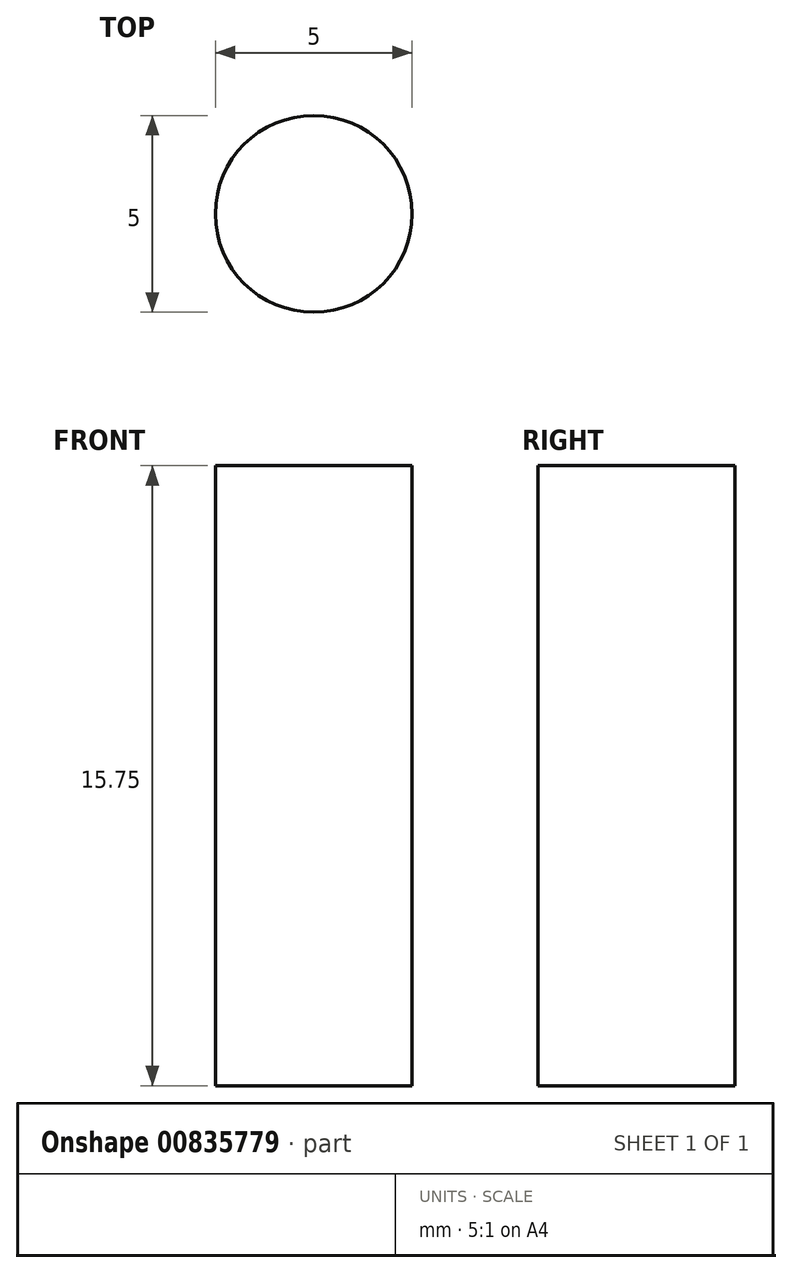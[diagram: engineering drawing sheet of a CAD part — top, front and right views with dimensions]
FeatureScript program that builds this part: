
annotation { "Feature Type Name" : "Feature", "Feature Type Description" : "" }
export const myFeature = defineFeature(function(context is Context, id is Id, definition is map)
    precondition{}
    {
        {
            var Q0;
            Q0=qCreatedBy(makeId("Top.planeOp"),FACE);
            var sketch = newSketch(context, id + "F0", { "sketchPlane" : qUnion([Q0])});
            skLineSegment(sketch, "E0.bottom", {"start": v(-18, 18.3) * mm, "end": v(18, 18.3) * mm, "construction": true});
            skLineSegment(sketch, "E0.top", {"start": v(-13, -18.3) * mm, "end": v(13, -18.3) * mm});
            skLineSegment(sketch, "E0.left", {"start": v(-18, 18.3) * mm, "end": v(-18, -13.3) * mm});
            skLineSegment(sketch, "E0.right", {"start": v(18, 18.3) * mm, "end": v(18, -13.3) * mm});
            skArc(sketch, "E1", {"start": v(18, 18.3) * mm, "mid": v(0, 36.3) * mm, "end": v(-18, 18.3) * mm});
            skLineSegment(sketch, "E2", {"start": v(-18, 0) * mm, "end": v(0, 0) * mm, "construction": true});
            skLineSegment(sketch, "E3", {"start": v(0, 0) * mm, "end": v(18, 0) * mm, "construction": true});
            skPoint(sketch, "E4", {"position": v(0, 36.3) * mm});
            skPoint(sketch, "E5.visualSharp", {"position": v(-18, -18.3) * mm});
            skArc(sketch, "E5.filletArc", {"start": v(-18, -13.3) * mm, "mid": v(-16.54, -16.84) * mm, "end": v(-13, -18.3) * mm});
            skPoint(sketch, "E6.visualSharp", {"position": v(18, -18.3) * mm});
            skArc(sketch, "E6.filletArc", {"start": v(13, -18.3) * mm, "mid": v(16.54, -16.84) * mm, "end": v(18, -13.3) * mm});
            skSolve(sketch);
        }
        {
            var Q0;
            Q0 = qSketchRegion(id + "F0", true);
            extrude(context, id + "F1", {"entities" : qUnion([Q0]), "depth" : 15.75 * mm, "offsetDistance" : 25 * mm});
        }
        {
            var Q0;
            Q0=makeQuery(id+"F1.opExtrude","CAP_FACE",FACE,{"disambiguationData":[OSD([sQuery(id+"F0.wireOp",EDGE,"E0.top"),sQuery(id+"F0.wireOp",EDGE,"E0.left"),sQuery(id+"F0.wireOp",EDGE,"E0.right"),sQuery(id+"F0.wireOp",EDGE,"E1")])],"isStart":false});
            var sketch = newSketch(context, id + "F2", { "sketchPlane" : qUnion([Q0])});
            skCircle(sketch, "E7", {"center": v(0, 27.3) * mm, "radius": 2.5 * mm});
            skCircle(sketch, "E8", {"center": v(11, 6.2) * mm, "radius": 2.5 * mm});
            skCircle(sketch, "E9.MirrorC", {"center": v(-11, 6.2) * mm, "radius": 2.5 * mm});
            skSolve(sketch);
        }
        {
            var Q0;
            Q0=makeQuery(id+"F2.imprint","IMPRINT",FACE,{"disambiguationData":[TD([[makeQuery(id+"F2.imprint","IMPRINT",EDGE,{"derivedFrom":sQuery(id+"F2.wireOp",EDGE,"E7")}),1.0]])]});
            var Q1;
            Q1=makeQuery(id+"F2.imprint","IMPRINT",FACE,{"disambiguationData":[TD([[makeQuery(id+"F2.imprint","IMPRINT",EDGE,{"derivedFrom":sQuery(id+"F2.wireOp",EDGE,"E9.MirrorC")}),-1.0]])]});
            var Q2;
            Q2=makeQuery(id+"F2.imprint","IMPRINT",FACE,{"disambiguationData":[TD([[makeQuery(id+"F2.imprint","IMPRINT",EDGE,{"derivedFrom":sQuery(id+"F2.wireOp",EDGE,"E8")}),1.0]])]});
            extrude(context, id + "F3", {"entities" : qUnion([Q0, Q1, Q2]), "operationType" : NewBodyOperationType.REMOVE, "endBound" : BoundingType.THROUGH_ALL, "oppositeDirection" : true, "depth" : 25 * mm, "offsetDistance" : 25 * mm});
        }
    });
